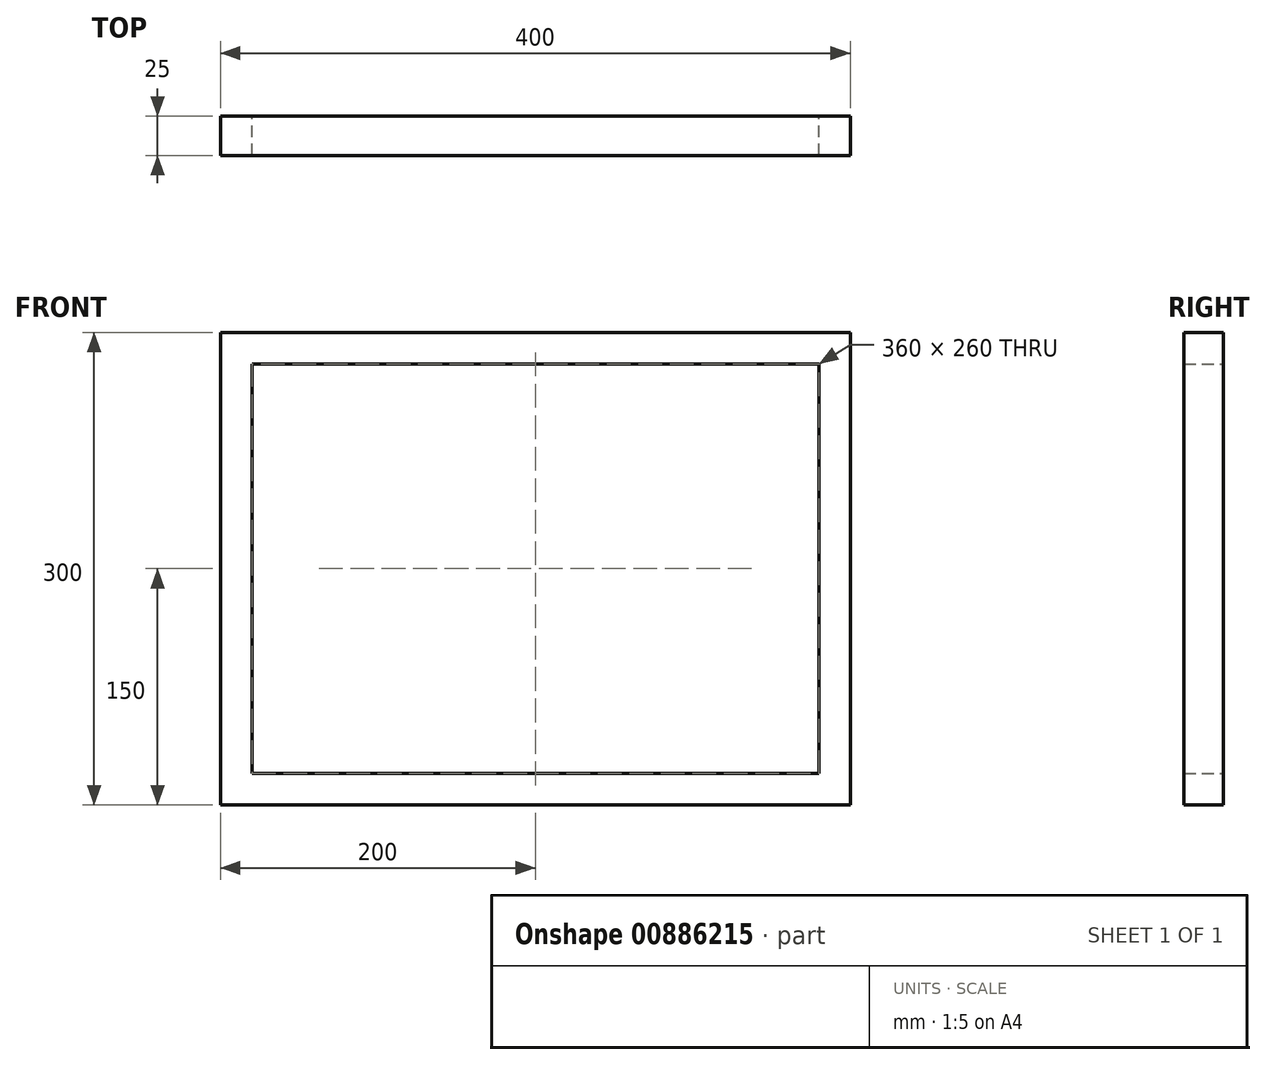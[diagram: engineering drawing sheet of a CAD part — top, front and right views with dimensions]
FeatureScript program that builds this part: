
annotation { "Feature Type Name" : "Feature", "Feature Type Description" : "" }
export const myFeature = defineFeature(function(context is Context, id is Id, definition is map)
    precondition{}
    {
        {
            var Q0;
            Q0=qCreatedBy(makeId("Front.planeOp"),FACE);
            var sketch = newSketch(context, id + "F0", { "sketchPlane" : qUnion([Q0])});
            skLineSegment(sketch, "E0.bottom", {"start": v(200, -150) * mm, "end": v(-200, -150) * mm});
            skLineSegment(sketch, "E0.top", {"start": v(200, 150) * mm, "end": v(-200, 150) * mm});
            skLineSegment(sketch, "E0.left", {"start": v(200, -150) * mm, "end": v(200, 150) * mm});
            skLineSegment(sketch, "E0.right", {"start": v(-200, -150) * mm, "end": v(-200, 150) * mm});
            skPoint(sketch, "E0.middle", {"position": v(0, 0) * mm});
            skLineSegment(sketch, "E1.bottom", {"start": v(180, -130) * mm, "end": v(-180, -130) * mm});
            skLineSegment(sketch, "E1.top", {"start": v(180, 130) * mm, "end": v(-180, 130) * mm});
            skLineSegment(sketch, "E1.left", {"start": v(180, -130) * mm, "end": v(180, 130) * mm});
            skLineSegment(sketch, "E1.right", {"start": v(-180, -130) * mm, "end": v(-180, 130) * mm});
            skSolve(sketch);
        }
        {
            var Q0;
            Q0 = qSketchRegion(id + "F0", true);
            extrude(context, id + "F1", {"entities" : qUnion([Q0]), "depth" : 25 * mm, "offsetDistance" : 25 * mm});
        }
    });
